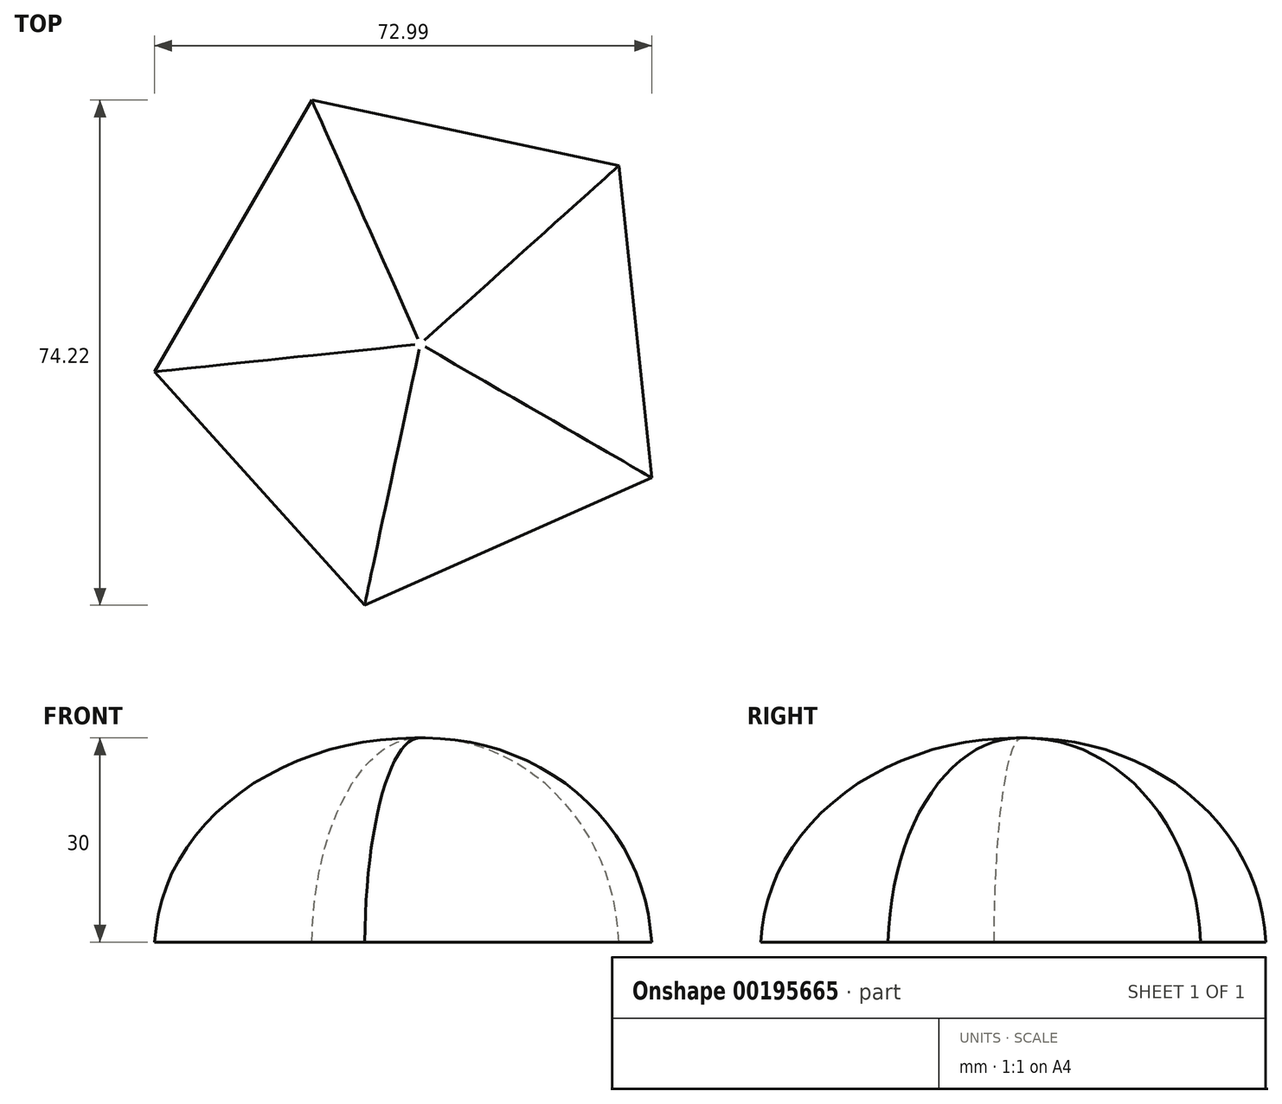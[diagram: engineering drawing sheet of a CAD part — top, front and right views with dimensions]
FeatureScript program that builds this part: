
annotation { "Feature Type Name" : "Feature", "Feature Type Description" : "" }
export const myFeature = defineFeature(function(context is Context, id is Id, definition is map)
    precondition{}
    {
        {
            var Q0;
            Q0=qCreatedBy(makeId("Top.planeOp"),FACE);
            var sketch = newSketch(context, id + "F0", { "sketchPlane" : qUnion([Q0])});
            skCircle(sketch, "E0.cCircle", {"center": v(0, 0) * mm, "radius": 31.74 * mm, "construction": true});
            skLineSegment(sketch, "E0.0", {"start": v(-39.02, -4.08) * mm, "end": v(-15.94, 35.85) * mm});
            skLineSegment(sketch, "E0.1", {"start": v(-15.94, 35.85) * mm, "end": v(29.17, 26.24) * mm});
            skLineSegment(sketch, "E0.2", {"start": v(29.17, 26.24) * mm, "end": v(33.97, -19.64) * mm});
            skLineSegment(sketch, "E0.3", {"start": v(33.97, -19.64) * mm, "end": v(-8.18, -38.37) * mm});
            skLineSegment(sketch, "E0.4", {"start": v(-8.18, -38.37) * mm, "end": v(-39.02, -4.08) * mm});
            skPoint(sketch, "E0.0.midPoint", {"position": v(-27.48, 15.89) * mm});
            skSolve(sketch);
        }
        {
            var Q0;
            Q0=makeQuery(id+"F0.imprint","IMPRINT",FACE,{"disambiguationData":[TD([[makeQuery(id+"F0.imprint","IMPRINT",EDGE,{"derivedFrom":sQuery(id+"F0.wireOp",EDGE,"E0.0")}),-1.0]])]});
            extrude(context, id + "F1", {"entities" : qUnion([Q0]), "depth" : 30 * mm});
        }
        {
            var Q0;
            Q0=makeQuery(id+"F1.opExtrude","CAP_FACE",FACE,{"disambiguationData":[OSD([sQuery(id+"F0.wireOp",EDGE,"E0.0"),sQuery(id+"F0.wireOp",EDGE,"E0.1"),sQuery(id+"F0.wireOp",EDGE,"E0.2"),sQuery(id+"F0.wireOp",EDGE,"E0.3"),sQuery(id+"F0.wireOp",EDGE,"E0.4")])],"isStart":false});
            fillet(context, id + "F2", {"entities" : qUnion([Q0]), "radius" : 31.1 * mm, "tangentPropagation" : true, "allowEdgeOverflow" : false});
        }
    });
